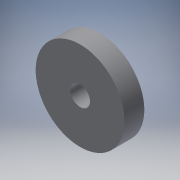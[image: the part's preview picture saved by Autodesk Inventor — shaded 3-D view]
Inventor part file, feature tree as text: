
AUTODESK INVENTOR PART (.ipt)
format: ipt  version: 2017 (Build 210142000, 142)  size: 96,768 bytes
history: native  units: in
note: dims shown in document units (in); Inventor stores cm internally (conversion verified against a paired STEP export)
features: extrude x1, sketch x1
ambient origin geometry x8: Origin, YZ Plane, XZ Plane, XY Plane, X Axis, Y Axis, Z Axis, Center Point
bodies: Solid1 (feature_tree)
feature tree (2):
  extrude  "Extrusion1"  Depth=0.3937in
  sketch  "Sketch1"  dims[d0=1.7717in d1=0.3937in d2=0.3937in d3=0.0in]
